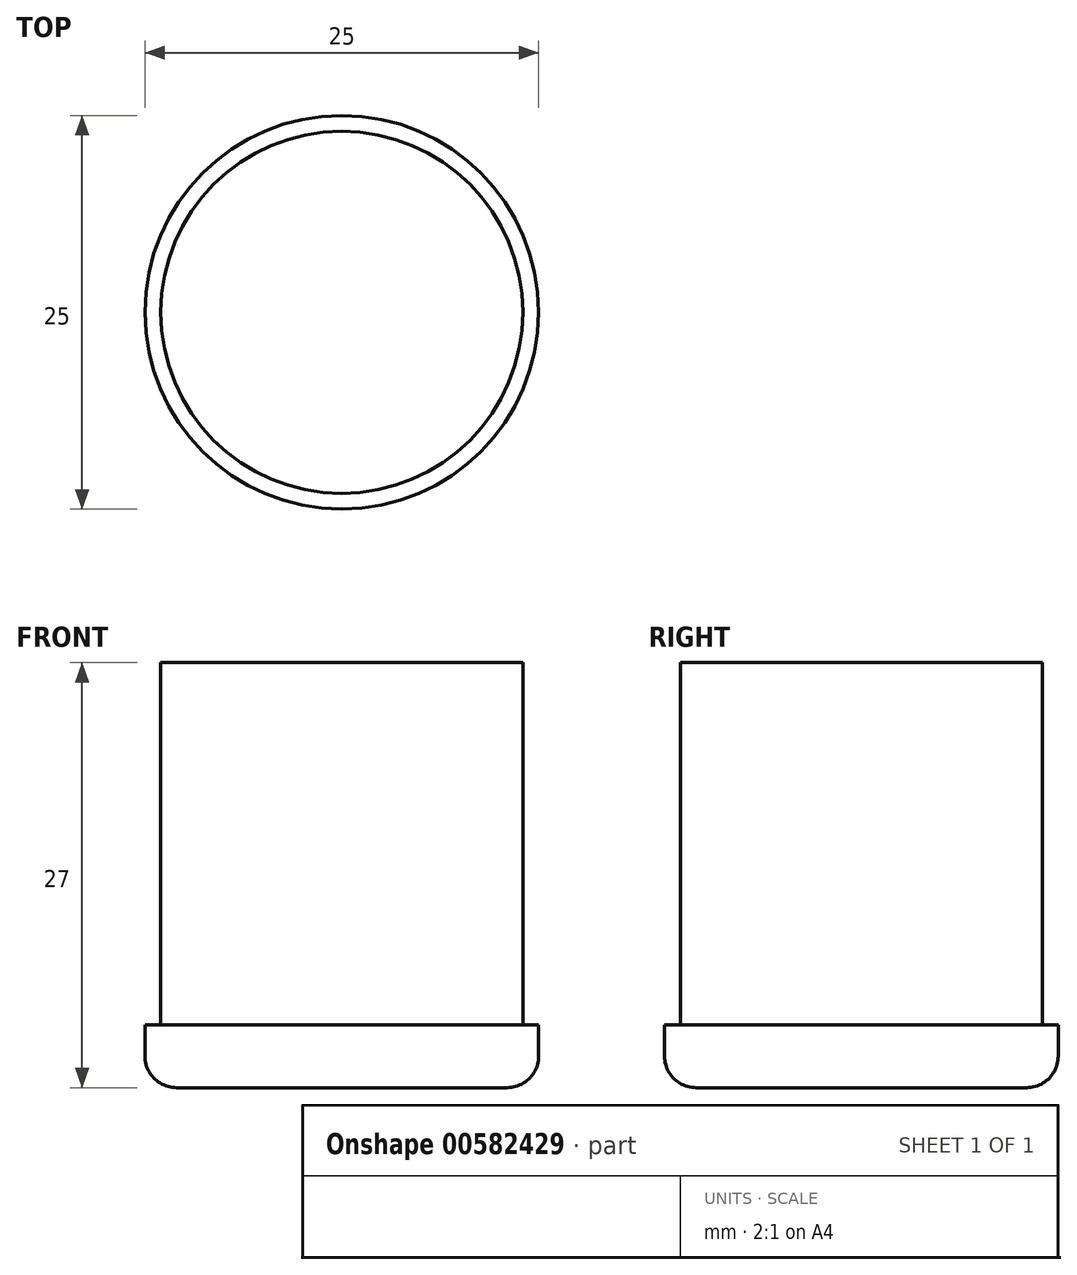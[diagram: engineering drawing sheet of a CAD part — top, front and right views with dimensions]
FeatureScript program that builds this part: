
annotation { "Feature Type Name" : "Feature", "Feature Type Description" : "" }
export const myFeature = defineFeature(function(context is Context, id is Id, definition is map)
    precondition{}
    {
        {
            assignVariable(context, id + "F0", {"name" : "za", "anyValue" : 4});
        }
        {
            assignVariable(context, id + "F1", {"name" : "Di", "anyValue" : 23});
        }
        {
            var Q0;
            Q0=qCreatedBy(makeId("Top.planeOp"),FACE);
            var sketch = newSketch(context, id + "F2", { "sketchPlane" : qUnion([Q0])});
            skCircle(sketch, "E0", {"center": v(0, 0) * mm, "radius": 12.5 * mm});
            skSolve(sketch);
        }
        {
            var Q0;
            Q0 = qSketchRegion(id + "F2", true);
            extrude(context, id + "F3", {"entities" : qUnion([Q0]), "depth" : (getVariable(context, 'za')) * mm, "offsetDistance" : 25 * mm});
        }
        {
            var Q0;
            Q0=makeQuery(id+"F3.opExtrude","CAP_FACE",FACE,{"disambiguationData":[OSD([sQuery(id+"F2.wireOp",EDGE,"E0")])],"isStart":false});
            var sketch = newSketch(context, id + "F4", { "sketchPlane" : qUnion([Q0])});
            skCircle(sketch, "E1", {"center": v(0, 0) * mm, "radius": 11.5 * mm});
            skSolve(sketch);
        }
        {
            var Q0;
            Q0 = qSketchRegion(id + "F4", true);
            extrude(context, id + "F5", {"entities" : qUnion([Q0]), "operationType" : NewBodyOperationType.ADD, "depth" : (getVariable(context, 'Di')) * mm, "offsetDistance" : 25 * mm});
        }
        {
            var Q0;
            Q0=makeQuery(id+"F3.opExtrude","CAP_EDGE",EDGE,{"disambiguationData":[OSD([sQuery(id+"F2.wireOp",EDGE,"E0")])],"isStart":true});
            fillet(context, id + "F6", {"entities" : qUnion([Q0]), "radius" : 2 * mm, "tangentPropagation" : true, "allowEdgeOverflow" : false});
        }
    });
